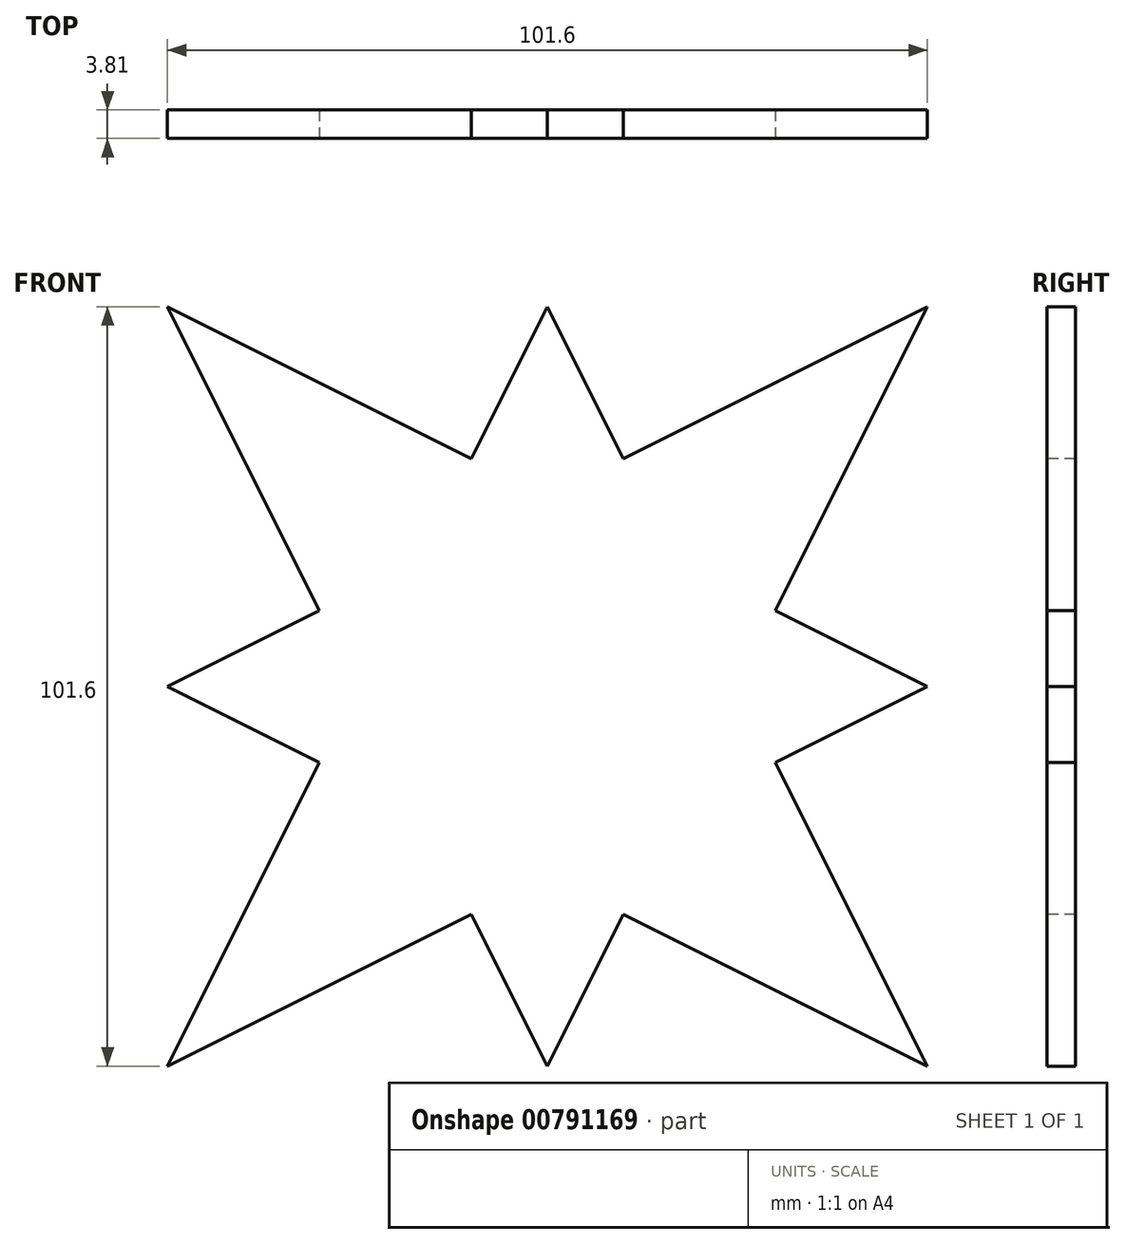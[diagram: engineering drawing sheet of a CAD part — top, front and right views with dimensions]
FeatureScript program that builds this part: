
annotation { "Feature Type Name" : "Feature", "Feature Type Description" : "" }
export const myFeature = defineFeature(function(context is Context, id is Id, definition is map)
    precondition{}
    {
        {
            var Q0;
            Q0=qCreatedBy(makeId("Front.planeOp"),FACE);
            var sketch = newSketch(context, id + "F0", { "sketchPlane" : qUnion([Q0])});
            skLineSegment(sketch, "E0.bottom", {"start": v(50.8, 50.8) * mm, "end": v(-50.8, 50.8) * mm});
            skLineSegment(sketch, "E0.top", {"start": v(50.8, -50.8) * mm, "end": v(-50.8, -50.8) * mm});
            skLineSegment(sketch, "E0.left", {"start": v(50.8, 50.8) * mm, "end": v(50.8, -50.8) * mm});
            skLineSegment(sketch, "E0.right", {"start": v(-50.8, 50.8) * mm, "end": v(-50.8, -50.8) * mm});
            skPoint(sketch, "E0.middle", {"position": v(0, 0) * mm});
            skSolve(sketch);
        }
        {
            var Q0;
            Q0=makeQuery(id+"F0.imprint","IMPRINT",FACE,{"disambiguationData":[TD([[makeQuery(id+"F0.imprint","IMPRINT",EDGE,{"derivedFrom":sQuery(id+"F0.wireOp",EDGE,"E0.bottom")}),1.0]])]});
            extrude(context, id + "F1", {"entities" : qUnion([Q0]), "depth" : 7.62 * mm, "offsetDistance" : 25.4 * mm});
        }
        {
            var Q0;
            Q0=makeQuery(id+"F1.opExtrude","CAP_FACE",FACE,{"disambiguationData":[OSD([sQuery(id+"F0.wireOp",EDGE,"E0.bottom"),sQuery(id+"F0.wireOp",EDGE,"E0.top"),sQuery(id+"F0.wireOp",EDGE,"E0.left"),sQuery(id+"F0.wireOp",EDGE,"E0.right")])],"isStart":false});
            var sketch = newSketch(context, id + "F2", { "sketchPlane" : qUnion([Q0])});
            skLineSegment(sketch, "E1", {"start": v(0, 50.8) * mm, "end": v(-50.8, -50.8) * mm});
            skLineSegment(sketch, "E2", {"start": v(-50.8, -50.8) * mm, "end": v(50.8, -50.8) * mm});
            skLineSegment(sketch, "E3", {"start": v(50.8, -50.8) * mm, "end": v(0, 50.8) * mm});
            skLineSegment(sketch, "E4", {"start": v(-50.8, 50.8) * mm, "end": v(0, -50.8) * mm});
            skLineSegment(sketch, "E5", {"start": v(0, -50.8) * mm, "end": v(50.8, 50.8) * mm});
            skLineSegment(sketch, "E6", {"start": v(50.8, 50.8) * mm, "end": v(-50.8, 50.8) * mm});
            skLineSegment(sketch, "E7", {"start": v(-50.8, 0) * mm, "end": v(50.8, -50.8) * mm});
            skLineSegment(sketch, "E8", {"start": v(50.8, 50.8) * mm, "end": v(-50.8, 0) * mm});
            skLineSegment(sketch, "E9", {"start": v(50.8, 0) * mm, "end": v(-50.8, -50.8) * mm});
            skLineSegment(sketch, "E10", {"start": v(-50.8, 50.8) * mm, "end": v(50.8, 0) * mm});
            skSolve(sketch);
        }
        {
            var Q0;
            {var subQ0=sQuery(id+"F2.wireOp",EDGE,"E10");var subQ1=sQuery(id+"F2.wireOp",EDGE,"E1");var subQ2=makeQuery(id+"F2.imprint","INTERSECT",VERTEX,{"derivedFrom":[subQ1,subQ0]});Q0=makeQuery(id+"F2.imprint","IMPRINT",FACE,{"disambiguationData":[TD([[makeQuery(id+"F2.imprint","IMPRINT",EDGE,{"disambiguationData":[TD([[subQ2,-1.0]])],"derivedFrom":subQ1}),-1.0]])]});}
            var Q1;
            {var subQ0=sQuery(id+"F2.wireOp",EDGE,"E3");var subQ5=sQuery(id+"F2.wireOp",EDGE,"E8");var subQ6=makeQuery(id+"F2.imprint","INTERSECT",VERTEX,{"derivedFrom":[subQ0,subQ5]});Q1=makeQuery(id+"F2.imprint","IMPRINT",FACE,{"disambiguationData":[TD([[makeQuery(id+"F2.imprint","IMPRINT",EDGE,{"disambiguationData":[TD([[subQ6,-1.0]])],"derivedFrom":subQ5}),-1.0]])]});}
            var Q2;
            {var subQ0=sQuery(id+"F2.wireOp",EDGE,"E10");var subQ1=sQuery(id+"F2.wireOp",EDGE,"E1");var subQ2=makeQuery(id+"F2.imprint","INTERSECT",VERTEX,{"derivedFrom":[subQ1,subQ0]});Q2=makeQuery(id+"F2.imprint","IMPRINT",FACE,{"disambiguationData":[TD([[makeQuery(id+"F2.imprint","IMPRINT",EDGE,{"disambiguationData":[TD([[subQ2,-1.0]])],"derivedFrom":subQ1}),1.0]])]});}
            var Q3;
            {var subQ0=sQuery(id+"F2.wireOp",EDGE,"E10");var subQ1=sQuery(id+"F2.wireOp",EDGE,"E3");var subQ2=makeQuery(id+"F2.imprint","INTERSECT",VERTEX,{"derivedFrom":[subQ1,subQ0]});Q3=makeQuery(id+"F2.imprint","IMPRINT",FACE,{"disambiguationData":[TD([[makeQuery(id+"F2.imprint","IMPRINT",EDGE,{"disambiguationData":[TD([[subQ2,-1.0]])],"derivedFrom":subQ1}),1.0]])]});}
            var Q4;
            {var subQ0=sQuery(id+"F2.wireOp",EDGE,"E10");var subQ1=sQuery(id+"F2.wireOp",EDGE,"E3");var subQ2=makeQuery(id+"F2.imprint","INTERSECT",VERTEX,{"derivedFrom":[subQ1,subQ0]});Q4=makeQuery(id+"F2.imprint","IMPRINT",FACE,{"disambiguationData":[TD([[makeQuery(id+"F2.imprint","IMPRINT",EDGE,{"disambiguationData":[TD([[subQ2,-1.0]])],"derivedFrom":subQ1}),-1.0]])]});}
            var Q5;
            {var subQ0=sQuery(id+"F2.wireOp",EDGE,"E9");var subQ1=sQuery(id+"F2.wireOp",EDGE,"E3");var subQ2=makeQuery(id+"F2.imprint","INTERSECT",VERTEX,{"derivedFrom":[subQ1,subQ0]});Q5=makeQuery(id+"F2.imprint","IMPRINT",FACE,{"disambiguationData":[TD([[makeQuery(id+"F2.imprint","IMPRINT",EDGE,{"disambiguationData":[TD([[subQ2,-1.0]])],"derivedFrom":subQ1}),-1.0]])]});}
            var Q6;
            {var subQ0=sQuery(id+"F2.wireOp",EDGE,"E7");var subQ5=sQuery(id+"F2.wireOp",EDGE,"E5");var subQ6=makeQuery(id+"F2.imprint","INTERSECT",VERTEX,{"derivedFrom":[subQ5,subQ0]});Q6=makeQuery(id+"F2.imprint","IMPRINT",FACE,{"disambiguationData":[TD([[makeQuery(id+"F2.imprint","IMPRINT",EDGE,{"disambiguationData":[TD([[subQ6,-1.0]])],"derivedFrom":subQ5}),-1.0]])]});}
            var Q7;
            {var subQ0=sQuery(id+"F2.wireOp",EDGE,"E5");var subQ5=sQuery(id+"F2.wireOp",EDGE,"E7");var subQ6=makeQuery(id+"F2.imprint","INTERSECT",VERTEX,{"derivedFrom":[subQ0,subQ5]});Q7=makeQuery(id+"F2.imprint","IMPRINT",FACE,{"disambiguationData":[TD([[makeQuery(id+"F2.imprint","IMPRINT",EDGE,{"disambiguationData":[TD([[subQ6,1.0]])],"derivedFrom":subQ5}),-1.0]])]});}
            var Q8;
            {var subQ3=sQuery(id+"F2.wireOp",EDGE,"E7");var subQ5=sQuery(id+"F2.wireOp",EDGE,"E4");var subQ6=makeQuery(id+"F2.imprint","INTERSECT",VERTEX,{"derivedFrom":[subQ5,subQ3]});Q8=makeQuery(id+"F2.imprint","IMPRINT",FACE,{"disambiguationData":[TD([[makeQuery(id+"F2.imprint","IMPRINT",EDGE,{"disambiguationData":[TD([[subQ6,-1.0]])],"derivedFrom":subQ5}),-1.0]])]});}
            var Q9;
            {var subQ0=sQuery(id+"F2.wireOp",EDGE,"E4");var subQ1=sQuery(id+"F2.wireOp",EDGE,"E1");var subQ2=makeQuery(id+"F2.imprint","INTERSECT",VERTEX,{"derivedFrom":[subQ1,subQ0]});Q9=makeQuery(id+"F2.imprint","IMPRINT",FACE,{"disambiguationData":[TD([[makeQuery(id+"F2.imprint","IMPRINT",EDGE,{"disambiguationData":[TD([[subQ2,-1.0]])],"derivedFrom":subQ1}),-1.0]])]});}
            var Q10;
            {var subQ0=sQuery(id+"F2.wireOp",EDGE,"E8");var subQ1=sQuery(id+"F2.wireOp",EDGE,"E1");var subQ2=makeQuery(id+"F2.imprint","INTERSECT",VERTEX,{"derivedFrom":[subQ1,subQ0]});Q10=makeQuery(id+"F2.imprint","IMPRINT",FACE,{"disambiguationData":[TD([[makeQuery(id+"F2.imprint","IMPRINT",EDGE,{"disambiguationData":[TD([[subQ2,-1.0]])],"derivedFrom":subQ1}),-1.0]])]});}
            var Q11;
            {var subQ7=sQuery(id+"F2.wireOp",EDGE,"E8");var subQ10=sQuery(id+"F2.wireOp",EDGE,"E1");var subQ15=makeQuery(id+"F2.imprint","INTERSECT",VERTEX,{"derivedFrom":[subQ10,subQ7]});Q11=makeQuery(id+"F2.imprint","IMPRINT",FACE,{"disambiguationData":[TD([[makeQuery(id+"F2.imprint","IMPRINT",EDGE,{"disambiguationData":[TD([[subQ15,-1.0]])],"derivedFrom":subQ10}),1.0]])]});}
            var Q12;
            {var subQ0=sQuery(id+"F2.wireOp",EDGE,"E7");var subQ1=sQuery(id+"F2.wireOp",EDGE,"E5");var subQ2=makeQuery(id+"F2.imprint","INTERSECT",VERTEX,{"derivedFrom":[subQ1,subQ0]});Q12=makeQuery(id+"F2.imprint","IMPRINT",FACE,{"disambiguationData":[TD([[makeQuery(id+"F2.imprint","IMPRINT",EDGE,{"disambiguationData":[TD([[subQ2,-1.0]])],"derivedFrom":subQ1}),1.0]])]});}
            var Q13;
            {var subQ0=sQuery(id+"F2.wireOp",EDGE,"E9");var subQ1=sQuery(id+"F2.wireOp",EDGE,"E3");var subQ2=makeQuery(id+"F2.imprint","INTERSECT",VERTEX,{"derivedFrom":[subQ1,subQ0]});Q13=makeQuery(id+"F2.imprint","IMPRINT",FACE,{"disambiguationData":[TD([[makeQuery(id+"F2.imprint","IMPRINT",EDGE,{"disambiguationData":[TD([[subQ2,-1.0]])],"derivedFrom":subQ1}),1.0]])]});}
            var Q14;
            {var subQ0=sQuery(id+"F2.wireOp",EDGE,"E5");var subQ1=sQuery(id+"F2.wireOp",EDGE,"E3");var subQ2=makeQuery(id+"F2.imprint","INTERSECT",VERTEX,{"derivedFrom":[subQ1,subQ0]});Q14=makeQuery(id+"F2.imprint","IMPRINT",FACE,{"disambiguationData":[TD([[makeQuery(id+"F2.imprint","IMPRINT",EDGE,{"disambiguationData":[TD([[subQ2,-1.0]])],"derivedFrom":subQ1}),-1.0]])]});}
            var Q15;
            {var subQ0=sQuery(id+"F2.wireOp",EDGE,"E4");var subQ1=sQuery(id+"F2.wireOp",EDGE,"E1");var subQ2=makeQuery(id+"F2.imprint","INTERSECT",VERTEX,{"derivedFrom":[subQ1,subQ0]});Q15=makeQuery(id+"F2.imprint","IMPRINT",FACE,{"disambiguationData":[TD([[makeQuery(id+"F2.imprint","IMPRINT",EDGE,{"disambiguationData":[TD([[subQ2,-1.0]])],"derivedFrom":subQ1}),1.0]])]});}
            var Q16;
            {var subQ0=sQuery(id+"F2.wireOp",EDGE,"E7");var subQ1=sQuery(id+"F2.wireOp",EDGE,"E4");var subQ2=makeQuery(id+"F2.imprint","INTERSECT",VERTEX,{"derivedFrom":[subQ1,subQ0]});Q16=makeQuery(id+"F2.imprint","IMPRINT",FACE,{"disambiguationData":[TD([[makeQuery(id+"F2.imprint","IMPRINT",EDGE,{"disambiguationData":[TD([[subQ2,-1.0]])],"derivedFrom":subQ1}),1.0]])]});}
            extrude(context, id + "F3", {"entities" : qUnion([Q0, Q1, Q2, Q3, Q4, Q5, Q6, Q7, Q8, Q9, Q10, Q11, Q12, Q13, Q14, Q15, Q16]), "operationType" : NewBodyOperationType.INTERSECT, "oppositeDirection" : true, "depth" : 3.8 * mm, "offsetDistance" : 25.4 * mm});
        }
    });
